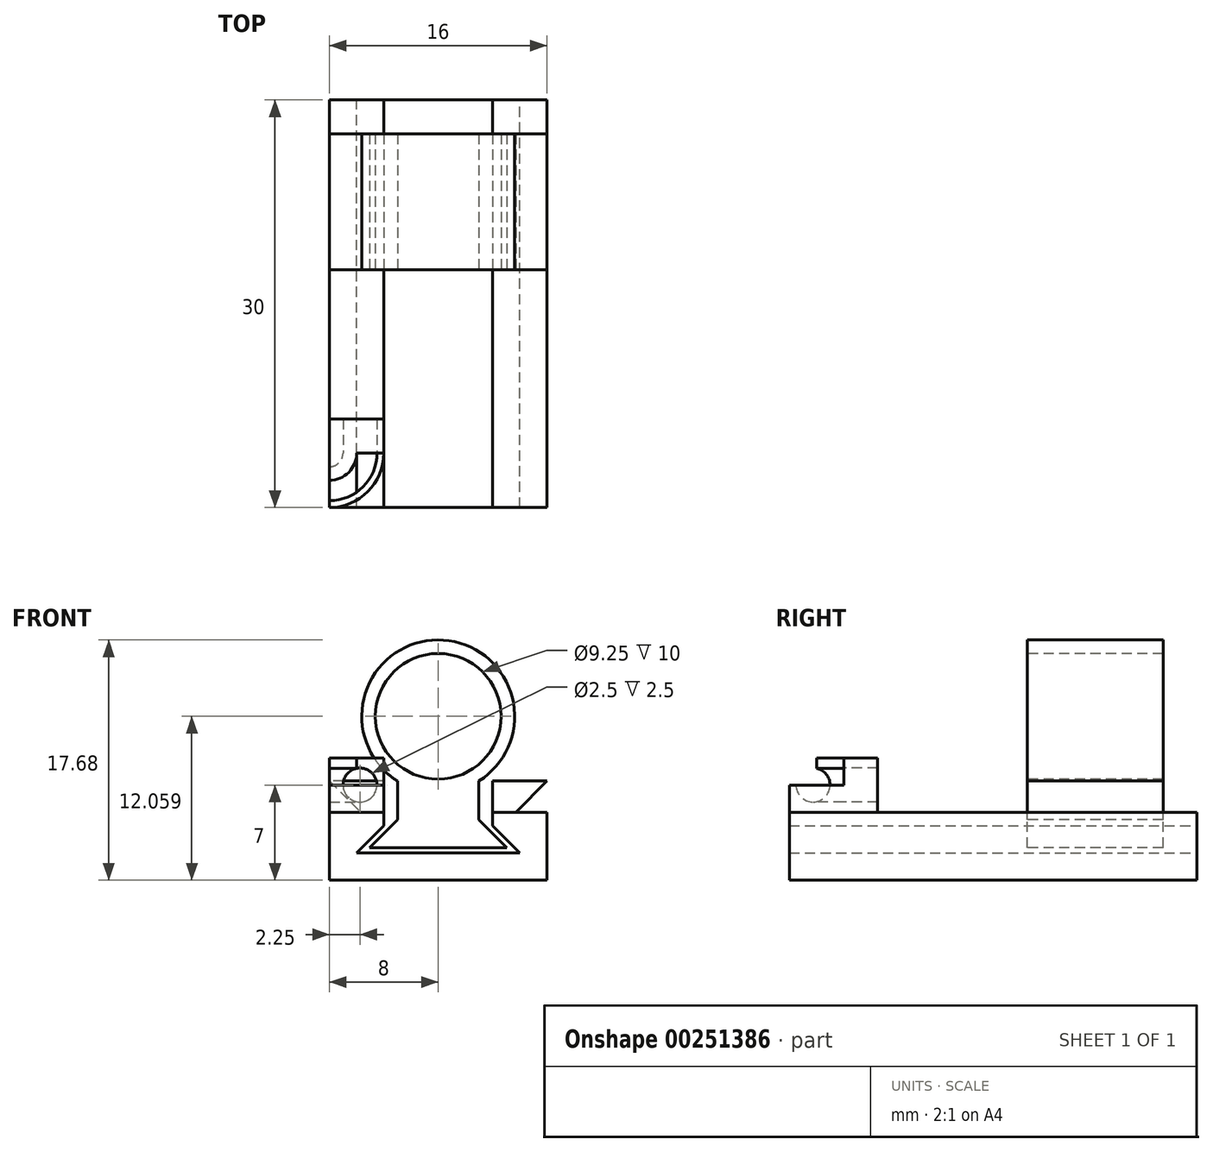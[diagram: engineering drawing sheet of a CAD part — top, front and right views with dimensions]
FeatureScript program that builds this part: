
annotation { "Feature Type Name" : "Feature", "Feature Type Description" : "" }
export const myFeature = defineFeature(function(context is Context, id is Id, definition is map)
    precondition{}
    {
        {
            var Q0;
            Q0=qCreatedBy(makeId("Front.planeOp"),FACE);
            var sketch = newSketch(context, id + "F0", { "sketchPlane" : qUnion([Q0])});
            skLineSegment(sketch, "E0", {"start": v(0, 0) * mm, "end": v(-6, 0) * mm});
            skLineSegment(sketch, "E1", {"start": v(-6, 0) * mm, "end": v(-4, 2) * mm});
            skLineSegment(sketch, "E2", {"start": v(-4, 2) * mm, "end": v(-4, 3) * mm});
            skLineSegment(sketch, "E3", {"start": v(-4, 3) * mm, "end": v(-8, 3) * mm});
            skLineSegment(sketch, "E4", {"start": v(-8, 3) * mm, "end": v(-8, -2) * mm});
            skLineSegment(sketch, "E5", {"start": v(-8, -2) * mm, "end": v(0, -2) * mm});
            skLineSegment(sketch, "E6.MirrorCS", {"start": v(0, 0) * mm, "end": v(6, 0) * mm});
            skLineSegment(sketch, "E7.MirrorCS", {"start": v(6, 0) * mm, "end": v(4, 2) * mm});
            skLineSegment(sketch, "E8.MirrorCS", {"start": v(4, 2) * mm, "end": v(4, 3) * mm});
            skLineSegment(sketch, "E9.MirrorCS", {"start": v(4, 3) * mm, "end": v(8, 3) * mm});
            skLineSegment(sketch, "E10.MirrorCS", {"start": v(8, 3) * mm, "end": v(8, -2) * mm});
            skLineSegment(sketch, "E11.MirrorCS", {"start": v(8, -2) * mm, "end": v(0, -2) * mm});
            skLineSegment(sketch, "E12", {"start": v(0, 0.4) * mm, "end": v(-5.03, 0.4) * mm});
            skLineSegment(sketch, "E13", {"start": v(-5.03, 0.4) * mm, "end": v(-3, 2.43) * mm});
            skLineSegment(sketch, "E14", {"start": v(-3, 2.43) * mm, "end": v(-3, 4.43) * mm});
            skLineSegment(sketch, "E15", {"start": v(-3, 4.43) * mm, "end": v(0, 4.43) * mm});
            skLineSegment(sketch, "E16.MirrorCS", {"start": v(3, 4.43) * mm, "end": v(0, 4.43) * mm});
            skLineSegment(sketch, "E17.MirrorCS", {"start": v(3, 2.43) * mm, "end": v(3, 4.43) * mm});
            skLineSegment(sketch, "E18.MirrorCS", {"start": v(5.03, 0.4) * mm, "end": v(3, 2.43) * mm});
            skLineSegment(sketch, "E19.MirrorCS", {"start": v(0, 0.4) * mm, "end": v(5.03, 0.4) * mm});
            skLineSegment(sketch, "E20", {"start": v(-3, 3.43) * mm, "end": v(3, 3.43) * mm, "construction": true});
            skCircle(sketch, "E21", {"center": v(0, 10.06) * mm, "radius": 4.63 * mm});
            skCircle(sketch, "E22", {"center": v(0, 10.06) * mm, "radius": 5.63 * mm});
            skLineSegment(sketch, "E23", {"start": v(-3, 4.43) * mm, "end": v(-3, 5.3) * mm});
            skLineSegment(sketch, "E24", {"start": v(3, 4.43) * mm, "end": v(3, 5.3) * mm});
            skLineSegment(sketch, "E25", {"start": v(-4, 3) * mm, "end": v(-4, 5.3) * mm});
            skLineSegment(sketch, "E26", {"start": v(-4, 5.3) * mm, "end": v(-8, 5.3) * mm});
            skLineSegment(sketch, "E27", {"start": v(-8, 5.3) * mm, "end": v(-5.7, 3) * mm});
            skLineSegment(sketch, "E28.MirrorCS", {"start": v(8, 5.3) * mm, "end": v(5.7, 3) * mm});
            skLineSegment(sketch, "E29.MirrorCS", {"start": v(4, 5.3) * mm, "end": v(8, 5.3) * mm});
            skLineSegment(sketch, "E30.MirrorCS", {"start": v(4, 3) * mm, "end": v(4, 5.3) * mm});
            skSolve(sketch);
        }
        {
            var Q0;
            Q0=makeQuery(id+"F0.imprint","IMPRINT",FACE,{"disambiguationData":[TD([[makeQuery(id+"F0.imprint","IMPRINT",EDGE,{"derivedFrom":sQuery(id+"F0.wireOp",EDGE,"E0")}),1.0]])]});
            extrude(context, id + "F1", {"entities" : qUnion([Q0]), "endBound" : BoundingType.SYMMETRIC, "depth" : 30 * mm});
        }
        {
            var Q0;
            Q0=makeQuery(id+"F0.imprint","IMPRINT",FACE,{"disambiguationData":[TD([[makeQuery(id+"F0.imprint","IMPRINT",EDGE,{"derivedFrom":sQuery(id+"F0.wireOp",EDGE,"E12")}),-1.0]])]});
            var Q1;
            {var subQ7=sQuery(id+"F0.wireOp",EDGE,"E15");var subQ8=sQuery(id+"F0.wireOp",EDGE,"E14");var subQ9=makeQuery(id+"F0.imprint","INTERSECT",VERTEX,{"derivedFrom":[subQ8,subQ7]});Q1=makeQuery(id+"F0.imprint","IMPRINT",FACE,{"disambiguationData":[TD([[makeQuery(id+"F0.imprint","IMPRINT",EDGE,{"disambiguationData":[TD([[subQ9,1.0]])],"derivedFrom":subQ8}),-1.0]])]});}
            var Q2;
            {var subQ7=sQuery(id+"F0.wireOp",EDGE,"E15");var subQ9=sQuery(id+"F0.wireOp",EDGE,"E14");var subQ10=makeQuery(id+"F0.imprint","INTERSECT",VERTEX,{"derivedFrom":[subQ9,subQ7]});Q2=makeQuery(id+"F0.imprint","IMPRINT",FACE,{"disambiguationData":[TD([[makeQuery(id+"F0.imprint","IMPRINT",EDGE,{"disambiguationData":[TD([[subQ10,1.0]])],"derivedFrom":subQ9}),1.0]])]});}
            var Q3;
            {var subQ0=sQuery(id+"F0.wireOp",EDGE,"E15");Q3=makeQuery(id+"F0.imprint","IMPRINT",FACE,{"disambiguationData":[TD([[makeQuery(id+"F0.imprint","IMPRINT",EDGE,{"derivedFrom":subQ0}),1.0]])]});}
            var Q4;
            Q4=makeQuery(id+"F0.imprint","IMPRINT",FACE,{"disambiguationData":[TD([[makeQuery(id+"F0.imprint","IMPRINT",EDGE,{"derivedFrom":sQuery(id+"F0.wireOp",EDGE,"E21")}),-1.0]])]});
            var Q5;
            {var subQ0=sQuery(id+"F0.wireOp",EDGE,"E16.MirrorCS");Q5=makeQuery(id+"F0.imprint","IMPRINT",FACE,{"disambiguationData":[TD([[makeQuery(id+"F0.imprint","IMPRINT",EDGE,{"derivedFrom":subQ0}),-1.0]])]});}
            extrude(context, id + "F2", {"entities" : qUnion([Q0, Q1, Q2, Q3, Q4, Q5]), "oppositeDirection" : true, "depth" : 12.5 * mm, "hasSecondDirection" : true, "secondDirectionOppositeDirection" : true, "secondDirectionDepth" : 2.5 * mm});
        }
        {
            var Q0;
            {var subQ0=sQuery(id+"F0.wireOp",EDGE,"E25");Q0=makeQuery(id+"F0.imprint","IMPRINT",FACE,{"disambiguationData":[TD([[makeQuery(id+"F0.imprint","IMPRINT",EDGE,{"derivedFrom":subQ0}),1.0]])]});}
            var Q1;
            {var subQ2=sQuery(id+"F0.wireOp",EDGE,"E28.MirrorCS");Q1=makeQuery(id+"F0.imprint","IMPRINT",FACE,{"disambiguationData":[TD([[makeQuery(id+"F0.imprint","IMPRINT",EDGE,{"derivedFrom":subQ2}),-1.0]])]});}
            extrude(context, id + "F3", {"entities" : qUnion([Q0, Q1]), "operationType" : NewBodyOperationType.ADD, "oppositeDirection" : true, "depth" : 12.5 * mm, "hasSecondDirection" : true, "secondDirectionOppositeDirection" : true, "secondDirectionDepth" : 2.5 * mm});
        }
        {
            var Q0;
            Q0=makeQuery(id+"F1.opExtrude","SWEPT_FACE",FACE,{"disambiguationData":[OSD([sQuery(id+"F0.wireOp",EDGE,"E4")])]});
            var sketch = newSketch(context, id + "F4", { "sketchPlane" : qUnion([Q0])});
            skPoint(sketch, "E31.0", {"position": v(15, 3) * mm});
            skLineSegment(sketch, "E32.bottom", {"start": v(15, 3) * mm, "end": v(11, 3) * mm});
            skLineSegment(sketch, "E32.top", {"start": v(15, 7) * mm, "end": v(11, 7) * mm});
            skLineSegment(sketch, "E32.left", {"start": v(15, 3) * mm, "end": v(15, 7) * mm});
            skLineSegment(sketch, "E32.right", {"start": v(11, 3) * mm, "end": v(11, 7) * mm});
            skCircle(sketch, "E33", {"center": v(13.25, 5) * mm, "radius": 1.25 * mm});
            skPoint(sketch, "E34", {"position": v(13, 7) * mm});
            skPoint(sketch, "E35", {"position": v(15, 5) * mm});
            skLineSegment(sketch, "E36", {"start": v(13, 7) * mm, "end": v(13, 6.22) * mm});
            skLineSegment(sketch, "E37", {"start": v(15, 5) * mm, "end": v(14.5, 5) * mm});
            skSolve(sketch);
        }
        {
            var Q0;
            {var subQ3=sQuery(id+"F4.wireOp",EDGE,"E32.bottom");Q0=makeQuery(id+"F4.imprint","IMPRINT",FACE,{"disambiguationData":[TD([[makeQuery(id+"F4.imprint","IMPRINT",EDGE,{"derivedFrom":subQ3}),-1.0]])]});}
            var Q1;
            Q1=sQuery(id+"F4.wireOp",EDGE,"E32.right");
            revolve(context, id + "F5", {"operationType" : NewBodyOperationType.ADD, "entities" : qUnion([Q0]), "axis" : qUnion([Q1]), "revolveType" : RevolveType.ONE_DIRECTION, "angle" : 90 * degree});
        }
        {
            var Q0;
            Q0=makeQuery(id+"F5.opRevolve","CAP_FACE",FACE,{"disambiguationData":[OSD([sQuery(id+"F4.wireOp",EDGE,"E32.bottom"),sQuery(id+"F4.wireOp",EDGE,"E32.top"),sQuery(id+"F4.wireOp",EDGE,"E32.left"),sQuery(id+"F4.wireOp",EDGE,"E32.right"),sQuery(id+"F4.wireOp",EDGE,"E33"),sQuery(id+"F4.wireOp",EDGE,"E36"),sQuery(id+"F4.wireOp",EDGE,"E37")])],"isStart":false});
            extrude(context, id + "F6", {"entities" : qUnion([Q0]), "operationType" : NewBodyOperationType.ADD, "depth" : 2.5 * mm});
        }
        {
            var Q0;
            Q0=makeQuery(id+"F6.opExtrude","CAP_FACE",FACE,{"disambiguationData":[OSD([sQuery(id+"F4.wireOp",EDGE,"E32.bottom"),sQuery(id+"F4.wireOp",EDGE,"E32.top"),sQuery(id+"F4.wireOp",EDGE,"E32.left"),sQuery(id+"F4.wireOp",EDGE,"E32.right"),sQuery(id+"F4.wireOp",EDGE,"E33"),sQuery(id+"F4.wireOp",EDGE,"E36"),sQuery(id+"F4.wireOp",EDGE,"E37")])],"isStart":false});
            var sketch = newSketch(context, id + "F7", { "sketchPlane" : qUnion([Q0])});
            skLineSegment(sketch, "E38", {"start": v(4, 5) * mm, "end": v(4, 7) * mm});
            skLineSegment(sketch, "E39", {"start": v(4, 7) * mm, "end": v(6, 7) * mm});
            skLineSegment(sketch, "E40", {"start": v(6, 7) * mm, "end": v(6, 6.22) * mm});
            skLineSegment(sketch, "E41", {"start": v(4, 5) * mm, "end": v(4.5, 5) * mm});
            skArc(sketch, "E42", {"start": v(6, 6.22) * mm, "mid": v(4.96, 5.97) * mm, "end": v(4.5, 5) * mm});
            skSolve(sketch);
        }
        {
            var Q0;
            Q0=makeQuery(id+"F7.imprint","IMPRINT",FACE,{"disambiguationData":[TD([[makeQuery(id+"F7.imprint","IMPRINT",EDGE,{"derivedFrom":sQuery(id+"F7.wireOp",EDGE,"E38")}),-1.0]])]});
            extrude(context, id + "F8", {"entities" : qUnion([Q0]), "operationType" : NewBodyOperationType.ADD, "oppositeDirection" : true, "depth" : 2.5 * mm});
        }
    });
